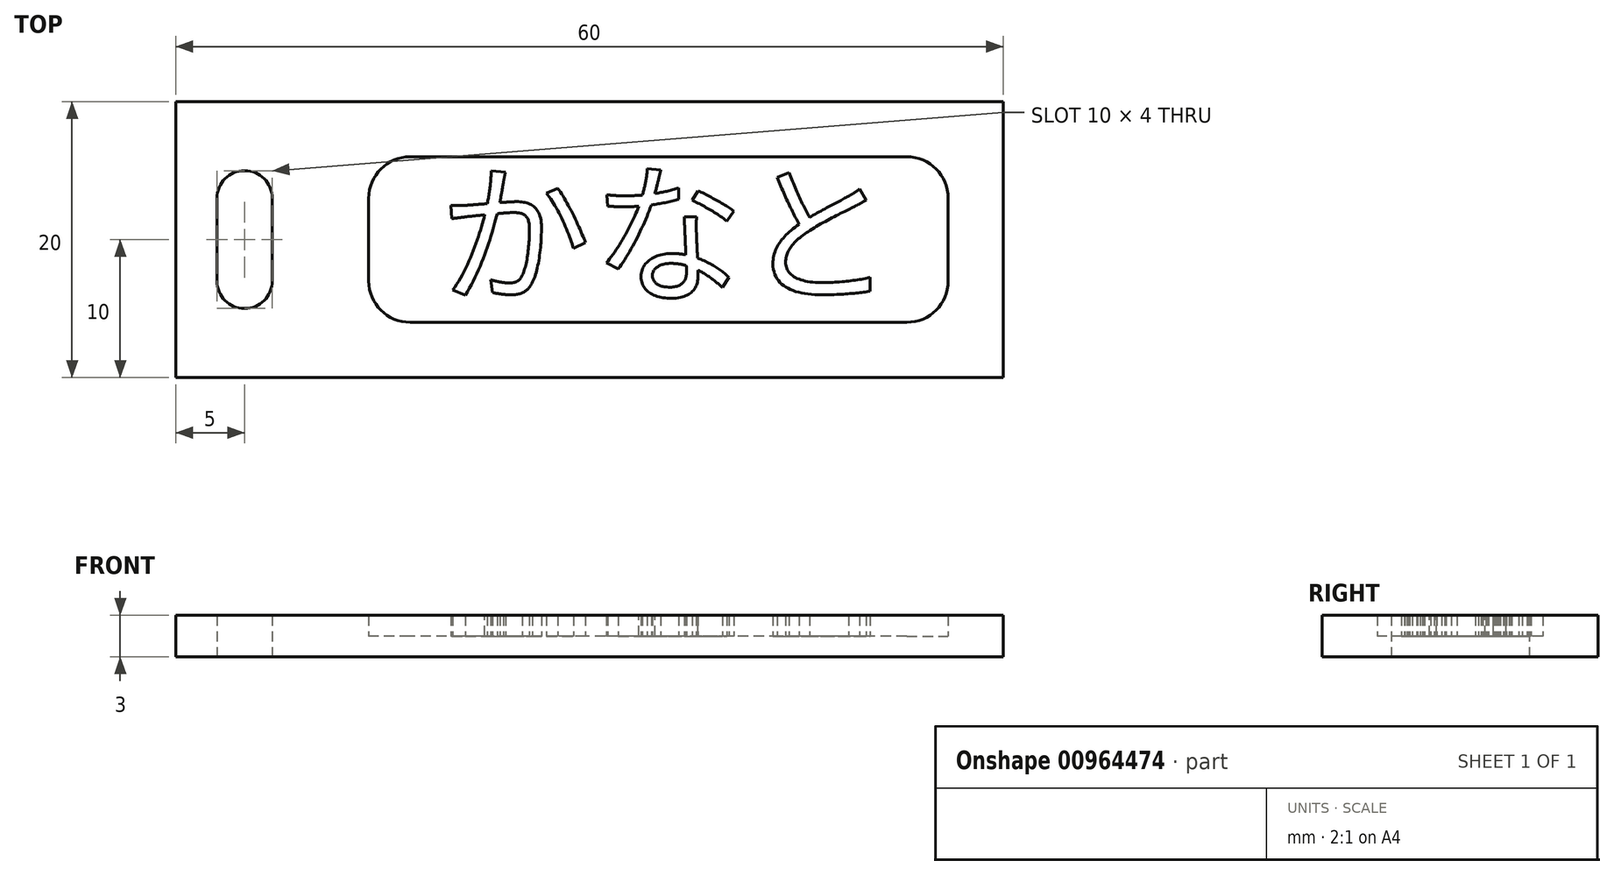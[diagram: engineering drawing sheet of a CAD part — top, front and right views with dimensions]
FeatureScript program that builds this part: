
annotation { "Feature Type Name" : "Feature", "Feature Type Description" : "" }
export const myFeature = defineFeature(function(context is Context, id is Id, definition is map)
    precondition{}
    {
        {
            var Q0;
            Q0=qCreatedBy(makeId("Top.planeOp"),FACE);
            var sketch = newSketch(context, id + "F0", { "sketchPlane" : qUnion([Q0])});
            skLineSegment(sketch, "E0.bottom", {"start": v(-25, -10) * mm, "end": v(25, -10) * mm});
            skLineSegment(sketch, "E0.top", {"start": v(-25, 10) * mm, "end": v(25, 10) * mm});
            skLineSegment(sketch, "E0.left", {"start": v(-25, -10) * mm, "end": v(-25, 10) * mm});
            skLineSegment(sketch, "E0.right", {"start": v(25, -10) * mm, "end": v(25, 10) * mm});
            skPoint(sketch, "E0.middle", {"position": v(0, 0) * mm});
            skLineSegment(sketch, "E1.bottom", {"start": v(-25, 10) * mm, "end": v(-35, 10) * mm});
            skLineSegment(sketch, "E1.top", {"start": v(-25, -10) * mm, "end": v(-35, -10) * mm});
            skLineSegment(sketch, "E1.left", {"start": v(-25, 10) * mm, "end": v(-25, -10) * mm});
            skLineSegment(sketch, "E1.right", {"start": v(-35, 10) * mm, "end": v(-35, -10) * mm});
            skPoint(sketch, "E1.middle", {"position": v(-30, 0) * mm});
            skLineSegment(sketch, "E2.bottom", {"start": v(-30, 5) * mm, "end": v(-30, 5) * mm});
            skLineSegment(sketch, "E2.top", {"start": v(-30, -5) * mm, "end": v(-30, -5) * mm});
            skLineSegment(sketch, "E2.left", {"start": v(-28, 3) * mm, "end": v(-28, -3) * mm});
            skLineSegment(sketch, "E2.right", {"start": v(-32, 3) * mm, "end": v(-32, -3) * mm});
            skPoint(sketch, "E3.visualSharp", {"position": v(-32, 5) * mm});
            skArc(sketch, "E3.filletArc", {"start": v(-30, 5) * mm, "mid": v(-31.41, 4.41) * mm, "end": v(-32, 3) * mm});
            skPoint(sketch, "E4.visualSharp", {"position": v(-28, 5) * mm});
            skArc(sketch, "E4.filletArc", {"start": v(-28, 3) * mm, "mid": v(-28.59, 4.41) * mm, "end": v(-30, 5) * mm});
            skPoint(sketch, "E5.visualSharp", {"position": v(-28, -5) * mm});
            skArc(sketch, "E5.filletArc", {"start": v(-30, -5) * mm, "mid": v(-28.59, -4.41) * mm, "end": v(-28, -3) * mm});
            skPoint(sketch, "E6.visualSharp", {"position": v(-32, -5) * mm});
            skArc(sketch, "E6.filletArc", {"start": v(-32, -3) * mm, "mid": v(-31.41, -4.41) * mm, "end": v(-30, -5) * mm});
            skSolve(sketch);
        }
        {
            var Q0;
            Q0 = qSketchRegion(id + "F0", true);
            extrude(context, id + "F1", {"entities" : qUnion([Q0]), "depth" : 3 * mm, "offsetDistance" : 25 * mm});
        }
        {
            var Q0;
            Q0=qCreatedBy(makeId("Top.planeOp"),FACE);
            var sketch = newSketch(context, id + "F2", { "sketchPlane" : qUnion([Q0])});
            skLineSegment(sketch, "E7.bottom", {"start": v(18, 6) * mm, "end": v(-18, 6) * mm});
            skLineSegment(sketch, "E7.top", {"start": v(18, -6) * mm, "end": v(-18, -6) * mm});
            skLineSegment(sketch, "E7.left", {"start": v(21, 3) * mm, "end": v(21, -3) * mm});
            skLineSegment(sketch, "E7.right", {"start": v(-21, 3) * mm, "end": v(-21, -3) * mm});
            skPoint(sketch, "E7.middle", {"position": v(0, 0) * mm});
            skPoint(sketch, "E8.visualSharp", {"position": v(-21, 6) * mm});
            skArc(sketch, "E8.filletArc", {"start": v(-18, 6) * mm, "mid": v(-20.12, 5.12) * mm, "end": v(-21, 3) * mm});
            skPoint(sketch, "E9.visualSharp", {"position": v(21, 6) * mm});
            skArc(sketch, "E9.filletArc", {"start": v(21, 3) * mm, "mid": v(20.12, 5.12) * mm, "end": v(18, 6) * mm});
            skPoint(sketch, "E10.visualSharp", {"position": v(-21, -6) * mm});
            skArc(sketch, "E10.filletArc", {"start": v(-21, -3) * mm, "mid": v(-20.12, -5.12) * mm, "end": v(-18, -6) * mm});
            skPoint(sketch, "E11.visualSharp", {"position": v(21, -6) * mm});
            skArc(sketch, "E11.filletArc", {"start": v(18, -6) * mm, "mid": v(20.12, -5.12) * mm, "end": v(21, -3) * mm});
            skSolve(sketch);
        }
        {
            var Q0;
            Q0 = qSketchRegion(id + "F2", true);
            extrude(context, id + "F3", {"entities" : qUnion([Q0]), "depth" : 3 * mm, "offsetDistance" : 25 * mm});
        }
        {
            var Q0;
            Q0=makeQuery(id+"F3.opExtrude","SWEPT_BODY",BODY,{"disambiguationData":[OSD([sQuery(id+"F2.wireOp",EDGE,"E7.bottom"),sQuery(id+"F2.wireOp",EDGE,"E7.top"),sQuery(id+"F2.wireOp",EDGE,"E7.left"),sQuery(id+"F2.wireOp",EDGE,"E7.right"),sQuery(id+"F2.wireOp",EDGE,"E8.filletArc"),sQuery(id+"F2.wireOp",EDGE,"E9.filletArc"),sQuery(id+"F2.wireOp",EDGE,"E10.filletArc"),sQuery(id+"F2.wireOp",EDGE,"E11.filletArc")])]});
            transform(context, id + "F4", {"entities" : qUnion([Q0]), "transformType" : TransformType.TRANSLATION_3D, "dx" : 0 * mm, "dy" : 0 * mm, "dz" : 1.5 * mm, "makeCopy" : false});
        }
        {
            var Q0;
            Q0=makeQuery(id+"F3.opExtrude","SWEPT_BODY",BODY,{"disambiguationData":[OSD([sQuery(id+"F2.wireOp",EDGE,"E7.bottom"),sQuery(id+"F2.wireOp",EDGE,"E7.top"),sQuery(id+"F2.wireOp",EDGE,"E7.left"),sQuery(id+"F2.wireOp",EDGE,"E7.right"),sQuery(id+"F2.wireOp",EDGE,"E8.filletArc"),sQuery(id+"F2.wireOp",EDGE,"E9.filletArc"),sQuery(id+"F2.wireOp",EDGE,"E10.filletArc"),sQuery(id+"F2.wireOp",EDGE,"E11.filletArc")])]});
            var Q1;
            Q1=makeQuery(id+"F1.opExtrude","SWEPT_BODY",BODY,{"disambiguationData":[OSD([sQuery(id+"F0.wireOp",EDGE,"E0.bottom"),sQuery(id+"F0.wireOp",EDGE,"E0.top"),sQuery(id+"F0.wireOp",EDGE,"E0.right"),sQuery(id+"F0.wireOp",EDGE,"E1.bottom"),sQuery(id+"F0.wireOp",EDGE,"E1.top"),sQuery(id+"F0.wireOp",EDGE,"E1.right"),sQuery(id+"F0.wireOp",EDGE,"E2.left"),sQuery(id+"F0.wireOp",EDGE,"E2.right"),sQuery(id+"F0.wireOp",EDGE,"E3.filletArc"),sQuery(id+"F0.wireOp",EDGE,"E4.filletArc"),sQuery(id+"F0.wireOp",EDGE,"E5.filletArc"),sQuery(id+"F0.wireOp",EDGE,"E6.filletArc")])]});
            booleanBodies(context, id + "F5", {"operationType" : BooleanOperationType.SUBTRACTION, "tools" : qUnion([Q0]), "targets" : qUnion([Q1])});
        }
        {
            var Q0;
            Q0=qCreatedBy(makeId("Top.planeOp"),FACE);
            var sketch = newSketch(context, id + "F6", { "sketchPlane" : qUnion([Q0])});
            skText(sketch, "E12", { "text": "かなと", "fontName": "NotoSansCJKjp-Regular.otf"});
            const initialGuessF6  = {"E12": [-0.01597, -0.00375, 1, 0, 0.008]};
            skSetInitialGuess(sketch, initialGuessF6);
            skSolve(sketch);
        }
        {
            var Q0;
            Q0 = qSketchRegion(id + "F6", true);
            extrude(context, id + "F7", {"entities" : qUnion([Q0]), "operationType" : NewBodyOperationType.ADD, "depth" : 3 * mm, "offsetDistance" : 25 * mm});
        }
    });
